# Revit family: Fire_Extinguisher_Cabinet-Whitehall-BestCare-WH1704-A
name_source: partatom
category: Specialty Equipment
revit_build: Autodesk Revit 2018 (Build: 20170223_1515(x64)
units: mm (PartAtom-declared; Revit-internal decimal feet)

## family parameters
Cut with Voids When Loaded = No
Host = Face
OmniClass Number = 23.65.70.17.27
OmniClass Title = Fire Extinguishers
Part Type = Normal
Room Calculation Point = No
Round Connector Dimension = Use Diameter
Shared = Yes

## types (1)
- WH1704-A
    Assembly Code = D4030200
    Body Material = Stainless Steel-Whitehall-Powder Coated White
    Default Elevation = 0"
    Description = BestCare® Ligature-Resistant Recessed Fire Extinguisher Cabinet
    Height = 26"
    Installation Type = Wall Mounted
    Length = 6"
    Manufacturer = Whitehall Manufacturing
    Material = Stainless Steel-Whitehall-Powder Coated White
    Model = WH1704-A
    Product Documentation Link = https://www.whitehallmfg.com
    Product Page URL = https://www.whitehallmfg.com
    URL = http://www.whitehallmfg.com
    Width = 11"

## geometry (parser evidence)
native form markers: Sweep x3
no freeform markers — native parametric forms only
